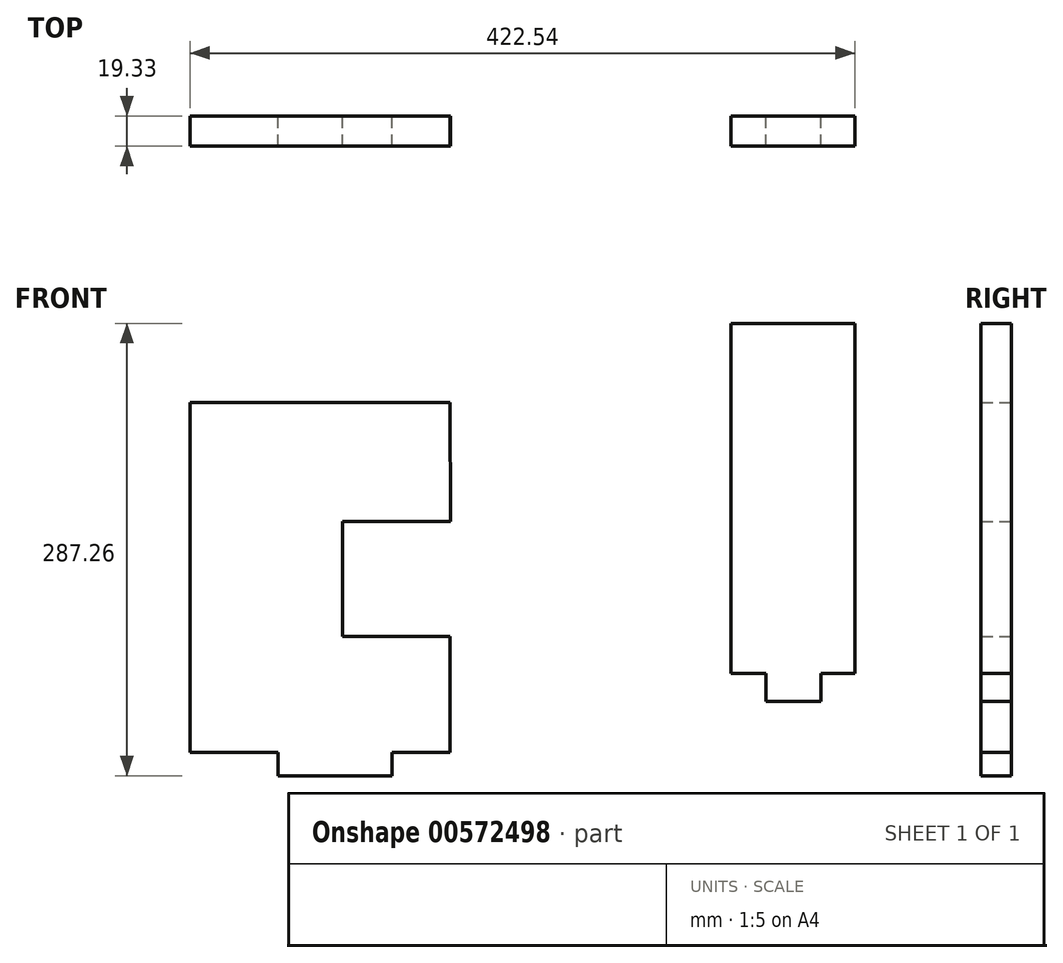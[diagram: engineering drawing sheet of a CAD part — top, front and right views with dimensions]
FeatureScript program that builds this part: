
annotation { "Feature Type Name" : "Feature", "Feature Type Description" : "" }
export const myFeature = defineFeature(function(context is Context, id is Id, definition is map)
    precondition{}
    {
        {
            var Q0;
            Q0=qCreatedBy(makeId("Front.planeOp"),FACE);
            var sketch = newSketch(context, id + "F0", { "sketchPlane" : qUnion([Q0])});
            skLineSegment(sketch, "E0", {"start": v(-56.15, 120.98) * mm, "end": v(-56.15, -101.27) * mm});
            skLineSegment(sketch, "E1", {"start": v(-56.15, 120.98) * mm, "end": v(108.95, 120.98) * mm});
            skLineSegment(sketch, "E2", {"start": v(-56.15, -101.27) * mm, "end": v(108.95, -101.27) * mm});
            skLineSegment(sketch, "E3", {"start": v(108.95, -101.27) * mm, "end": v(108.95, -27.5) * mm});
            skLineSegment(sketch, "E4", {"start": v(108.95, -27.5) * mm, "end": v(40.85, -27.5) * mm});
            skLineSegment(sketch, "E5", {"start": v(40.85, -27.5) * mm, "end": v(40.85, 45.65) * mm});
            skLineSegment(sketch, "E6", {"start": v(40.85, 45.65) * mm, "end": v(109.32, 45.65) * mm});
            skLineSegment(sketch, "E7", {"start": v(109.32, 45.65) * mm, "end": v(108.95, 120.98) * mm});
            skLineSegment(sketch, "E8", {"start": v(287.65, -50.92) * mm, "end": v(366.39, -50.92) * mm});
            skLineSegment(sketch, "E9", {"start": v(287.65, -50.92) * mm, "end": v(287.65, 171.33) * mm});
            skLineSegment(sketch, "E10", {"start": v(366.39, -50.92) * mm, "end": v(366.39, 171.33) * mm});
            skLineSegment(sketch, "E11", {"start": v(287.65, 171.33) * mm, "end": v(366.39, 171.33) * mm});
            skLineSegment(sketch, "E12.bottom", {"start": v(0, -101.27) * mm, "end": v(72.14, -101.27) * mm});
            skLineSegment(sketch, "E12.top", {"start": v(0, -115.93) * mm, "end": v(72.14, -115.93) * mm});
            skLineSegment(sketch, "E12.left", {"start": v(0, -101.27) * mm, "end": v(0, -115.93) * mm});
            skLineSegment(sketch, "E12.right", {"start": v(72.14, -101.27) * mm, "end": v(72.14, -115.93) * mm});
            skLineSegment(sketch, "E13", {"start": v(309.74, -50.92) * mm, "end": v(309.74, -68.85) * mm});
            skLineSegment(sketch, "E14", {"start": v(309.74, -68.85) * mm, "end": v(344.62, -68.85) * mm});
            skLineSegment(sketch, "E15", {"start": v(344.62, -68.85) * mm, "end": v(344.62, -50.92) * mm});
            skSolve(sketch);
        }
        {
            var Q0;
            Q0 = qSketchRegion(id + "F0", true);
            extrude(context, id + "F1", {"entities" : qUnion([Q0]), "depth" : 19.33 * mm, "offsetDistance" : 25.4 * mm});
        }
    });
